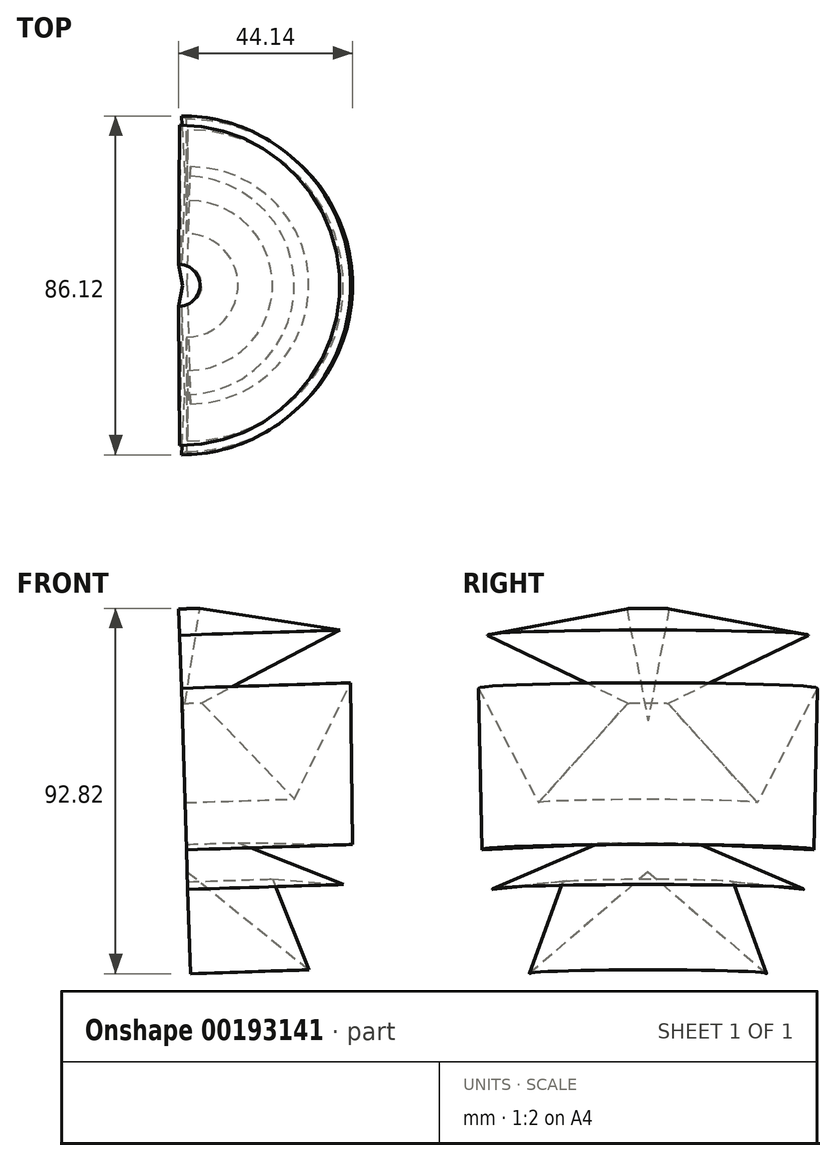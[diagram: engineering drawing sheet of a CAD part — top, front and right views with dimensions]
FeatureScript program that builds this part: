
annotation { "Feature Type Name" : "Feature", "Feature Type Description" : "" }
export const myFeature = defineFeature(function(context is Context, id is Id, definition is map)
    precondition{}
    {
        {
            var Q0;
            Q0=qCreatedBy(makeId("Front.planeOp"),FACE);
            var sketch = newSketch(context, id + "F0", { "sketchPlane" : qUnion([Q0])});
            skLineSegment(sketch, "E0", {"start": v(13.85, -22.85) * mm, "end": v(44.77, -47.78) * mm});
            skLineSegment(sketch, "E1", {"start": v(44.77, -47.78) * mm, "end": v(35.54, -24.7) * mm});
            skLineSegment(sketch, "E2", {"start": v(35.54, -24.7) * mm, "end": v(53.55, -26.08) * mm});
            skLineSegment(sketch, "E3", {"start": v(53.55, -26.08) * mm, "end": v(26.77, -15.46) * mm});
            skLineSegment(sketch, "E4", {"start": v(26.77, -15.46) * mm, "end": v(55.85, -15.93) * mm});
            skLineSegment(sketch, "E5", {"start": v(55.85, -15.93) * mm, "end": v(55.4, 25.16) * mm});
            skLineSegment(sketch, "E6", {"start": v(55.4, 25.16) * mm, "end": v(41.08, -4.39) * mm});
            skLineSegment(sketch, "E7", {"start": v(41.08, -4.39) * mm, "end": v(17.54, 20.08) * mm});
            skLineSegment(sketch, "E8", {"start": v(17.54, 20.08) * mm, "end": v(52.62, 38.54) * mm});
            skLineSegment(sketch, "E9", {"start": v(52.62, 38.54) * mm, "end": v(17.08, 44.08) * mm});
            skLineSegment(sketch, "E10", {"start": v(17.08, 44.08) * mm, "end": v(12.62, 15.47) * mm});
            skLineSegment(sketch, "E11", {"start": v(12.62, 15.47) * mm, "end": v(13.85, -22.85) * mm});
            skSolve(sketch);
        }
        {
            var Q0;
            Q0=makeQuery(id+"F0.imprint","IMPRINT",FACE,{"disambiguationData":[TD([[makeQuery(id+"F0.imprint","IMPRINT",EDGE,{"derivedFrom":sQuery(id+"F0.wireOp",EDGE,"E0")}),1.0]])]});
            var Q1;
            Q1=sQuery(id+"F0.wireOp",EDGE,"E11");
            var Q2;
            Q2=sQuery(id+"F0.wireOp",EDGE,"E11");
            revolve(context, id + "F1", {"entities" : qUnion([Q0]), "surfaceEntities" : qUnion([Q1]), "axis" : qUnion([Q2]), "revolveType" : RevolveType.SYMMETRIC, "angle" : 180 * degree});
        }
    });
